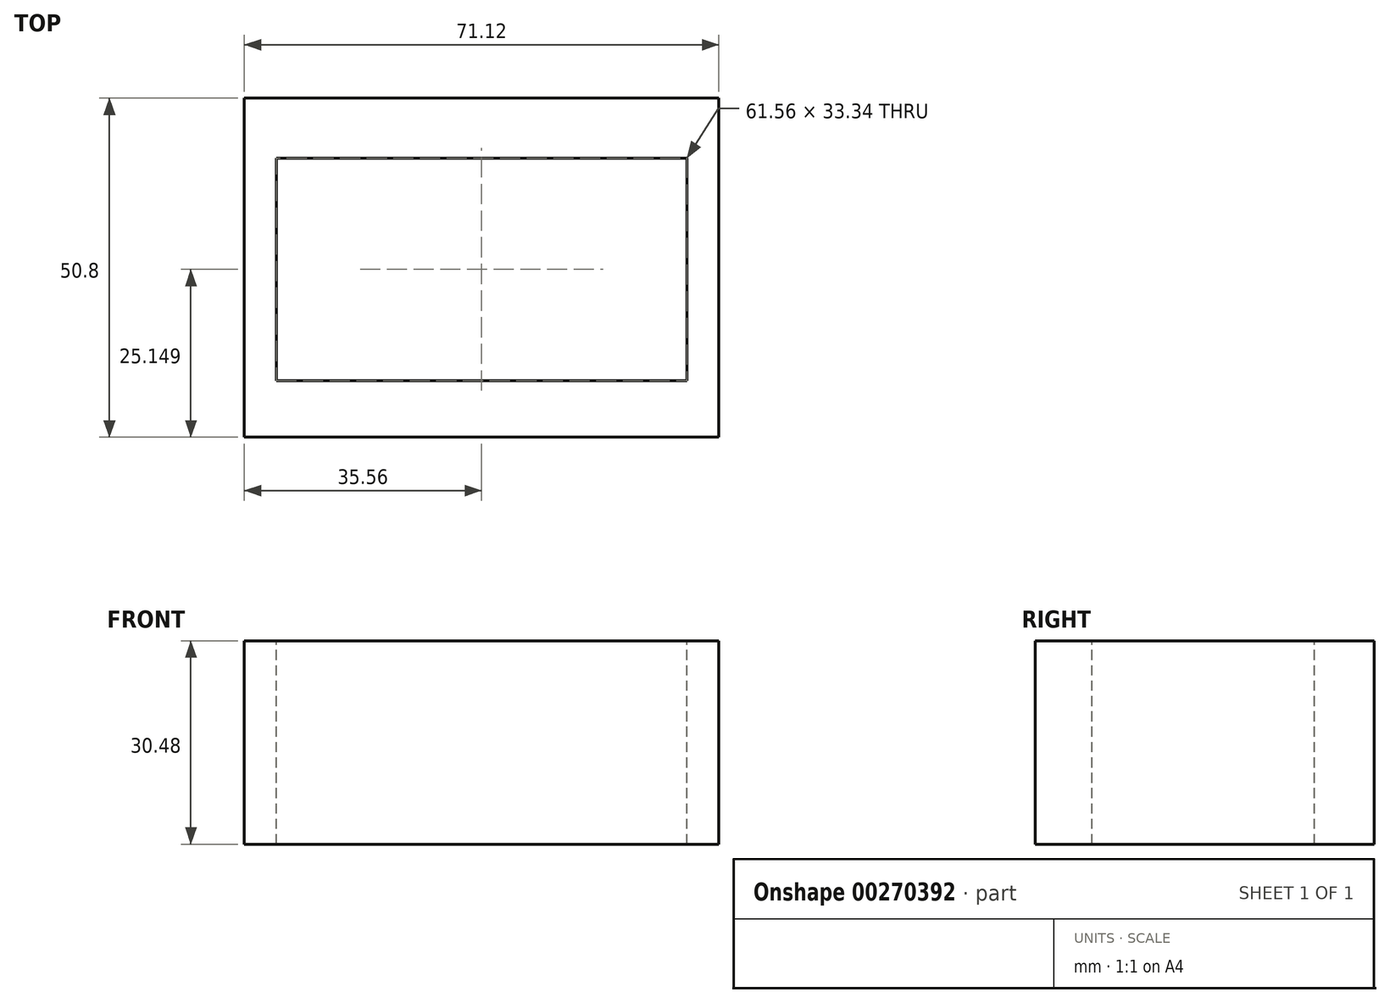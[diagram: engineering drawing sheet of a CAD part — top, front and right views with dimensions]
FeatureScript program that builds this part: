
annotation { "Feature Type Name" : "Feature", "Feature Type Description" : "" }
export const myFeature = defineFeature(function(context is Context, id is Id, definition is map)
    precondition{}
    {
        {
            var Q0;
            Q0=qCreatedBy(makeId("Front.planeOp"),FACE);
            var sketch = newSketch(context, id + "F0", { "sketchPlane" : qUnion([Q0])});
            skLineSegment(sketch, "E0.bottom", {"start": v(35.56, -15.24) * mm, "end": v(-35.56, -15.24) * mm});
            skLineSegment(sketch, "E0.top", {"start": v(35.56, 15.24) * mm, "end": v(-35.56, 15.24) * mm});
            skLineSegment(sketch, "E0.left", {"start": v(35.56, -15.24) * mm, "end": v(35.56, 15.24) * mm});
            skLineSegment(sketch, "E0.right", {"start": v(-35.56, -15.24) * mm, "end": v(-35.56, 15.24) * mm});
            skPoint(sketch, "E0.middle", {"position": v(0, 0) * mm});
            skSolve(sketch);
        }
        {
            var Q0;
            Q0 = qSketchRegion(id + "F0", true);
            extrude(context, id + "F1", {"entities" : qUnion([Q0]), "depth" : 50.8 * mm});
        }
        {
            var Q0;
            Q0=makeQuery(id+"F1.opExtrude","SWEPT_FACE",FACE,{"disambiguationData":[OSD([sQuery(id+"F0.wireOp",EDGE,"E0.top")])]});
            var sketch = newSketch(context, id + "F2", { "sketchPlane" : qUnion([Q0])});
            skLineSegment(sketch, "E1.bottom", {"start": v(30.78, -42.32) * mm, "end": v(-30.78, -42.32) * mm});
            skLineSegment(sketch, "E1.top", {"start": v(30.78, -8.98) * mm, "end": v(-30.78, -8.98) * mm});
            skLineSegment(sketch, "E1.left", {"start": v(30.78, -42.32) * mm, "end": v(30.78, -8.98) * mm});
            skLineSegment(sketch, "E1.right", {"start": v(-30.78, -42.32) * mm, "end": v(-30.78, -8.98) * mm});
            skPoint(sketch, "E1.middle", {"position": v(0, -25.65) * mm});
            skSolve(sketch);
        }
        {
            var Q0;
            Q0=makeQuery(id+"F2.imprint","IMPRINT",FACE,{"disambiguationData":[TD([[makeQuery(id+"F2.imprint","IMPRINT",EDGE,{"derivedFrom":sQuery(id+"F2.wireOp",EDGE,"E1.bottom")}),-1.0]])]});
            extrude(context, id + "F3", {"entities" : qUnion([Q0]), "operationType" : NewBodyOperationType.REMOVE, "oppositeDirection" : true, "depth" : 30.48 * mm});
        }
    });
